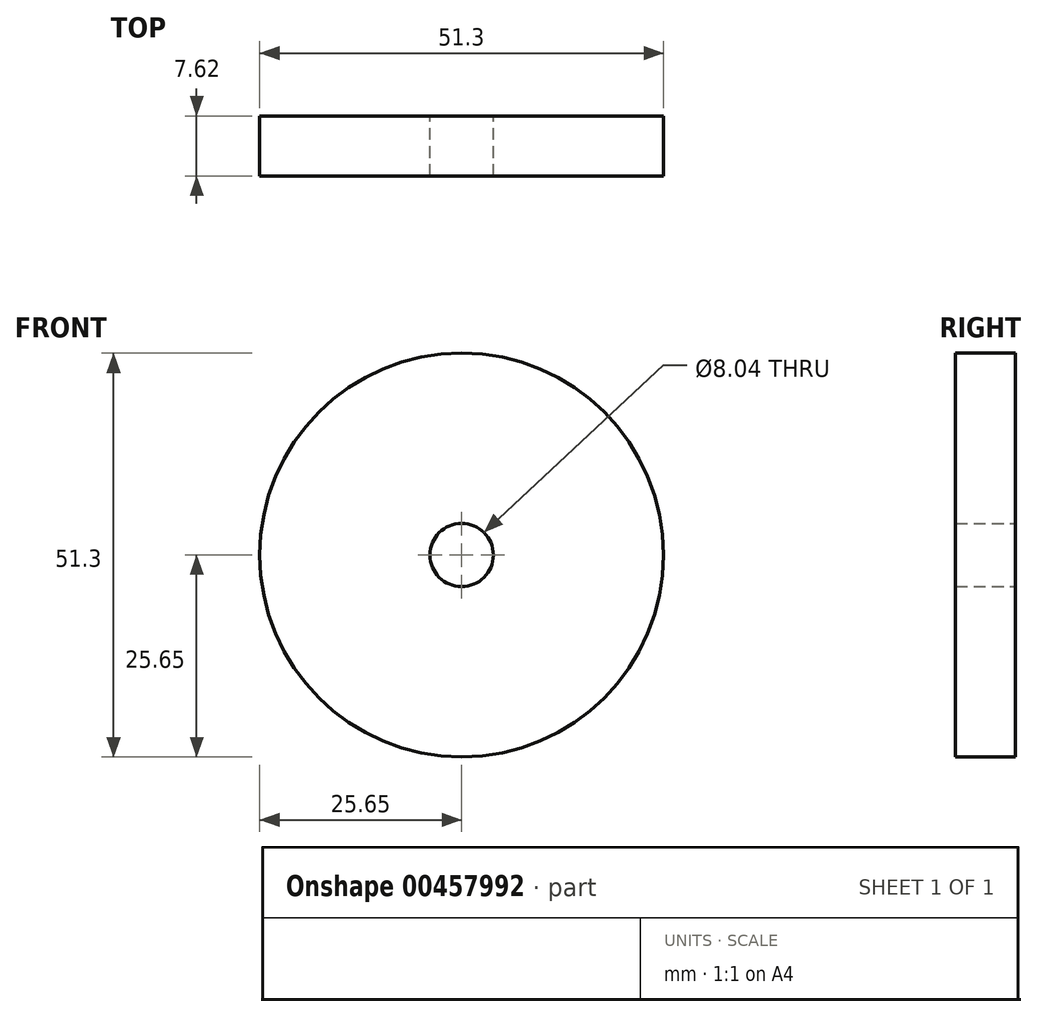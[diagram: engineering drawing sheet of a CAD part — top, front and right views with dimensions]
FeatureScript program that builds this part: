
annotation { "Feature Type Name" : "Feature", "Feature Type Description" : "" }
export const myFeature = defineFeature(function(context is Context, id is Id, definition is map)
    precondition{}
    {
        {
            var Q0;
            Q0=qCreatedBy(makeId("Front.planeOp"),FACE);
            var sketch = newSketch(context, id + "F0", { "sketchPlane" : qUnion([Q0])});
            skCircle(sketch, "E0", {"center": v(-29.4, 22.14) * mm, "radius": 25.65 * mm});
            skCircle(sketch, "E1", {"center": v(-29.4, 22.14) * mm, "radius": 4.02 * mm});
            skSolve(sketch);
        }
        {
            var Q0;
            Q0=makeQuery(id+"F0.imprint","IMPRINT",FACE,{"disambiguationData":[TD([[makeQuery(id+"F0.imprint","IMPRINT",EDGE,{"derivedFrom":sQuery(id+"F0.wireOp",EDGE,"E0")}),1.0]])]});
            extrude(context, id + "F1", {"entities" : qUnion([Q0]), "depth" : 7.62 * mm});
        }
    });
